# Revit family: PRD_AR_TltRllHldrs_STRATOSToiletRollHolder_STRX671E_STRX672E
name_source: partatom
category: Specialty Equipment
revit_build: Autodesk Revit 2018 (Build: 20190510_1515(x64)
units: mm (PartAtom-declared; Revit-internal decimal feet)

## family parameters
Cut with Voids When Loaded = Yes
Host = Face
OmniClass Number = 23.40.20.21.17
OmniClass Title = Paper Towel Dispensers, Disposal Units
Part Type = Normal
Room Calculation Point = No
Round Connector Dimension = Use Diameter
Shared = No

## types (2) — shared parameters
AssetType = Fixed
Category = Pr_40_20_76_88, Toilet roll holders
Default Elevation = 650 mm  [stored 2.13255 ft]
DurationUnit = year
Features = stainless steel, surface satin finished
FillingQuantity = 2
FillingQuantityUom = Rolls
Finish = satin finished
IfcExportAs = IfcFurnitureType
IfcExportType = USERDEFINED
IntegralAccessories = incl. stainless steel screws and dowels
IsBuiltIn = TRUE
Lock = Key-lock
MainColor = stainless steel
Manufacturer = KWC Group AG
ManufacturerName = KWC Group AG
ManufacturerURL = www.kwc.com
Material = stainless steel
MaterialCode = 1.4301
MaterialThickness = 1.50 mm
MaximumDepthDiameterOfConsumable = 120.00 mm
NBSDescription = Toilet roll holders
NBSReference = 45-35-72/368
NominalDepth = 142 mm  [stored 0.465879 ft]
NominalHeight = 331 mm  [stored 1.08596 ft]
NominalWidth = 183 mm
ProductInformation = https://pim.kwc.com
RollHolderMaterial = PRD_AR_StainlessSteel_SatinFinished
Size = 183 x 331 x 142 mm
Style = roll holder
SurfaceTreatment = InoxPlus (anti fingerprint)
ToiletRollMaterial = PRD_AR_ToiletRoll
TypeOfFixing = Screw
TypeOfMounting = Recessed mounting
URL = www.kwc.com
Uniclass2015Code = Pr_40_20_76_88
Uniclass2015Title = Toilet roll holders
Uniclass2015Version = Products v1.10
Version = 1
WarrantyDurationUnit = year

## per-type parameters (varying)
| type | BIMObjectName | Description | GrossWeight | MaximumWidthOfConsumable | ModelNumber | Name | NetWeight | Spindle |
| STRX671E | PRD_AR_ToiletRollHolders_STRATOSToiletRollHolder_STRX671E | Double toilet roll holder for recessed mounting, stainless steel, surface satin finished, front with InoxPlus surface refinement for the reduction of finger marks and better cleaning characteristics (easy to clean), material thickness 1.5 mm, curved front cover with inspection window, cylinder lock with KWC standard key, for 2 rolls with max. Ø 120 mm, second roll will be released after consumption of first roll, without spindles, inclusive stainless steel screws and dowels. | 3.87 kg | 115.00 mm | 2000057396 | Toilet roll holder STRX671E | 3.51 kg | No |
| STRX672E | PRD_AR_ToiletRollHolders_STRATOSToiletRollHolder_STRX672E | Double toilet roll holder with spindle system for recessed mounting, stainless steel, surface satin finished, front with InoxPlus surface refinement for the reduction of finger marks and better cleaning characteristics (easy to clean), material thickness 1.5 mm, curved front cover with inspection window, cylinder lock with KWC standard key, for 2 rolls with max. Ø 120 mm, second roll will be released after consumption of first roll, reserve roll not visible, inclusive stainless steel screws and dowels. | 3.92 kg | 100.00 mm | 2000057400 | Toilet roll holder STRX672E | 3.64 kg | Yes |

note: column(s) folded — value = type name in every type: Model, ModelReference, Type

note: [stored X ft] marks values corroborated as IEEE doubles in the binary element streams (Revit-internal decimal feet)

## geometry (parser evidence)
native form markers: Sweep x6
no freeform markers — native parametric forms only
